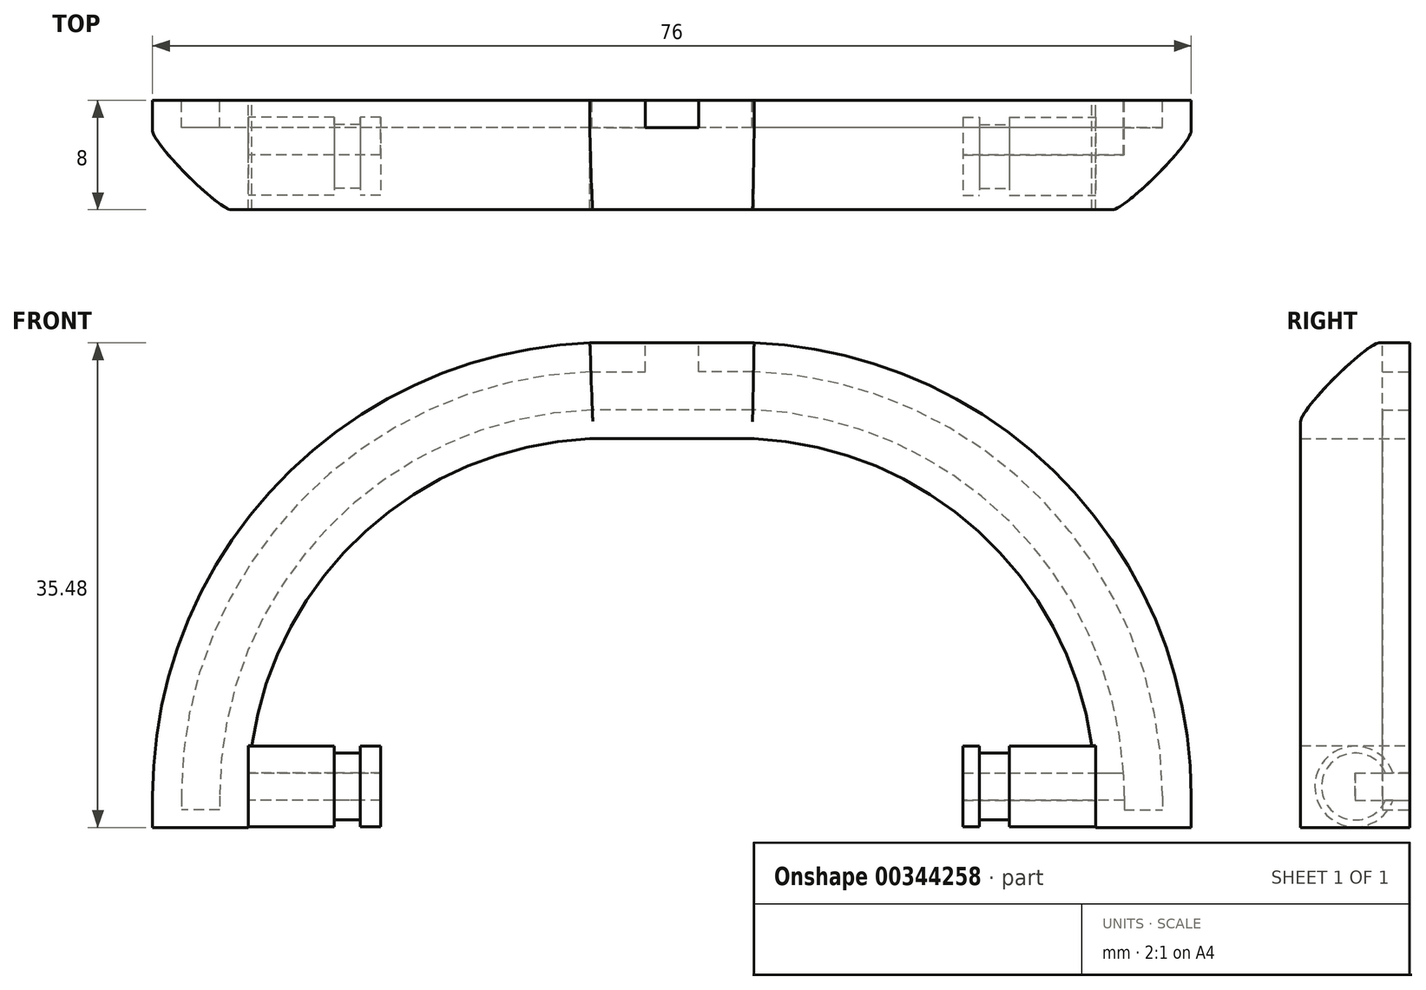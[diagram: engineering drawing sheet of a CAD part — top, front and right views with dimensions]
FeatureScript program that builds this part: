
annotation { "Feature Type Name" : "Feature", "Feature Type Description" : "" }
export const myFeature = defineFeature(function(context is Context, id is Id, definition is map)
    precondition{}
    {
        {
            var Q0;
            Q0=qCreatedBy(makeId("Front.planeOp"),FACE);
            var sketch = newSketch(context, id + "F0", { "sketchPlane" : qUnion([Q0])});
            skLineSegment(sketch, "E0.top", {"start": v(-4.75, 30.97) * mm, "end": v(4.75, 30.97) * mm});
            skPoint(sketch, "E0.middle", {"position": v(0, 0) * mm});
            skPoint(sketch, "E1", {"position": v(0, -2.5) * mm});
            skLineSegment(sketch, "E2", {"start": v(-38, -35.7) * mm, "end": v(-38, -38) * mm});
            skLineSegment(sketch, "E3", {"start": v(38, -35.7) * mm, "end": v(38, -38) * mm});
            skPoint(sketch, "E4.visualSharp", {"position": v(-38, -2.5) * mm});
            skArc(sketch, "E4.filletArc", {"start": v(-6, -2.52) * mm, "mid": v(-28.7, -12.65) * mm, "end": v(-38, -35.7) * mm});
            skPoint(sketch, "E5.visualSharp", {"position": v(38, -2.5) * mm});
            skArc(sketch, "E5.filletArc", {"start": v(38, -35.7) * mm, "mid": v(28.7, -12.66) * mm, "end": v(6.03, -2.52) * mm});
            skLineSegment(sketch, "E6", {"start": v(-31, -32) * mm, "end": v(-31, -38) * mm});
            skLineSegment(sketch, "E7", {"start": v(-38, -38) * mm, "end": v(-31, -38) * mm});
            skLineSegment(sketch, "E8", {"start": v(-4.75, 30.97) * mm, "end": v(-4.75, 9.5) * mm});
            skLineSegment(sketch, "E9", {"start": v(4.75, 9.47) * mm, "end": v(4.75, 30.97) * mm});
            skLineSegment(sketch, "E10.0", {"start": v(6.03, -2.52) * mm, "end": v(6, 9.48) * mm});
            skLineSegment(sketch, "E11.0", {"start": v(-6, 9.5) * mm, "end": v(-6, -2.52) * mm});
            skLineSegment(sketch, "E12", {"start": v(-6, 9.5) * mm, "end": v(-4.75, 9.5) * mm});
            skLineSegment(sketch, "E13", {"start": v(4.75, 9.47) * mm, "end": v(6, 9.48) * mm});
            skLineSegment(sketch, "E14", {"start": v(-6.02, -9.53) * mm, "end": v(6.02, -9.53) * mm});
            skLineSegment(sketch, "E15", {"start": v(-6, -2.52) * mm, "end": v(6.03, -2.52) * mm});
            skArc(sketch, "E16.0", {"start": v(-6.02, -9.53) * mm, "mid": v(-22.42, -16.31) * mm, "end": v(-30.74, -32) * mm});
            skLineSegment(sketch, "E17", {"start": v(-31, -32) * mm, "end": v(-30.74, -32) * mm});
            skLineSegment(sketch, "E18.MirrorCS", {"start": v(31, -32) * mm, "end": v(30.74, -32) * mm});
            skLineSegment(sketch, "E19.MirrorCS", {"start": v(38, -38) * mm, "end": v(31, -38) * mm});
            skLineSegment(sketch, "E20.MirrorCS", {"start": v(31, -32) * mm, "end": v(31, -38) * mm});
            skArc(sketch, "E21.MirrorCS", {"start": v(6.02, -9.53) * mm, "mid": v(22.42, -16.31) * mm, "end": v(30.74, -32) * mm});
            skSolve(sketch);
        }
        {
            var Q0;
            Q0=makeQuery(id+"F0.imprint","IMPRINT",FACE,{"disambiguationData":[TD([[makeQuery(id+"F0.imprint","IMPRINT",EDGE,{"derivedFrom":sQuery(id+"F0.wireOp",EDGE,"E2")}),1.0]])]});
            extrude(context, id + "F1", {"entities" : qUnion([Q0]), "depth" : 8 * mm});
        }
        {
            var Q0;
            Q0=makeQuery(id+"F1.opExtrude","CAP_EDGE",EDGE,{"disambiguationData":[OSD([sQuery(id+"F0.wireOp",EDGE,"E5.filletArc")])],"isStart":false});
            var Q1;
            Q1=makeQuery(id+"F1.opExtrude","CAP_EDGE",EDGE,{"disambiguationData":[OSD([sQuery(id+"F0.wireOp",EDGE,"E4.filletArc")])],"isStart":false});
            var Q2;
            Q2=makeQuery(id+"F1.opExtrude","CAP_EDGE",EDGE,{"disambiguationData":[OSD([sQuery(id+"F0.wireOp",EDGE,"E3")])],"isStart":false});
            var Q3;
            Q3=makeQuery(id+"F1.opExtrude","CAP_EDGE",EDGE,{"disambiguationData":[OSD([sQuery(id+"F0.wireOp",EDGE,"E2")])],"isStart":false});
            fillet(context, id + "F2", {"entities" : qUnion([Q0, Q1, Q2, Q3]), "radius" : 5.75 * mm, "tangentPropagation" : true, "rho" : 0.12, "crossSection" : FilletCrossSection.CONIC, "allowEdgeOverflow" : false});
        }
        {
            var Q0;
            Q0=makeQuery(id+"F1.opExtrude","SWEPT_FACE",FACE,{"disambiguationData":[OSD([sQuery(id+"F0.wireOp",EDGE,"E20.MirrorCS")])]});
            var sketch = newSketch(context, id + "F3", { "sketchPlane" : qUnion([Q0])});
            skLineSegment(sketch, "E22", {"start": v(0, -32) * mm, "end": v(8, -38) * mm, "construction": true});
            skCircle(sketch, "E23", {"center": v(4, -35) * mm, "radius": 2.95 * mm});
            skCircle(sketch, "E24", {"center": v(4, -35) * mm, "radius": 2.45 * mm});
            skSolve(sketch);
        }
        {
            var Q0;
            Q0=makeQuery(id+"F3.imprint","IMPRINT",FACE,{"disambiguationData":[TD([[makeQuery(id+"F3.imprint","IMPRINT",EDGE,{"derivedFrom":sQuery(id+"F3.wireOp",EDGE,"E23")}),1.0]])]});
            extrude(context, id + "F4", {"entities" : qUnion([Q0]), "operationType" : NewBodyOperationType.ADD, "depth" : 6.3 * mm});
        }
        {
            var Q0;
            Q0=makeQuery(id+"F3.imprint","IMPRINT",FACE,{"disambiguationData":[TD([[makeQuery(id+"F3.imprint","IMPRINT",EDGE,{"derivedFrom":sQuery(id+"F3.wireOp",EDGE,"E24")}),1.0]])]});
            extrude(context, id + "F5", {"entities" : qUnion([Q0]), "operationType" : NewBodyOperationType.ADD, "depth" : 9.7 * mm});
        }
        {
            var Q0;
            Q0=makeQuery(id+"F3.imprint","IMPRINT",FACE,{"disambiguationData":[TD([[makeQuery(id+"F3.imprint","IMPRINT",EDGE,{"derivedFrom":sQuery(id+"F3.wireOp",EDGE,"E23")}),1.0]])]});
            extrude(context, id + "F6", {"entities" : qUnion([Q0]), "operationType" : NewBodyOperationType.ADD, "depth" : 9.7 * mm, "hasSecondDirection" : true, "secondDirectionOppositeDirection" : false, "secondDirectionDepth" : 8.5 * mm});
        }
        {
            var Q0;
            Q0=makeQuery(id+"F1.opExtrude","SWEPT_FACE",FACE,{"disambiguationData":[OSD([sQuery(id+"F0.wireOp",EDGE,"E6")])]});
            var sketch = newSketch(context, id + "F7", { "sketchPlane" : qUnion([Q0])});
            skLineSegment(sketch, "E25", {"start": v(-8, -32) * mm, "end": v(0, -38) * mm, "construction": true});
            skCircle(sketch, "E26", {"center": v(-4, -35) * mm, "radius": 2.95 * mm});
            skCircle(sketch, "E27", {"center": v(-4, -35) * mm, "radius": 2.45 * mm});
            skSolve(sketch);
        }
        {
            var Q0;
            Q0=makeQuery(id+"F7.imprint","IMPRINT",FACE,{"disambiguationData":[TD([[makeQuery(id+"F7.imprint","IMPRINT",EDGE,{"derivedFrom":sQuery(id+"F7.wireOp",EDGE,"E26")}),1.0]])]});
            extrude(context, id + "F8", {"entities" : qUnion([Q0]), "operationType" : NewBodyOperationType.ADD, "depth" : 9.7 * mm, "hasSecondDirection" : true, "secondDirectionOppositeDirection" : false, "secondDirectionDepth" : 8.2 * mm});
        }
        {
            var Q0;
            Q0=makeQuery(id+"F7.imprint","IMPRINT",FACE,{"disambiguationData":[TD([[makeQuery(id+"F7.imprint","IMPRINT",EDGE,{"derivedFrom":sQuery(id+"F7.wireOp",EDGE,"E27")}),1.0]])]});
            extrude(context, id + "F9", {"entities" : qUnion([Q0]), "operationType" : NewBodyOperationType.ADD, "depth" : 9.7 * mm});
        }
        {
            var Q0;
            Q0=makeQuery(id+"F7.imprint","IMPRINT",FACE,{"disambiguationData":[TD([[makeQuery(id+"F7.imprint","IMPRINT",EDGE,{"derivedFrom":sQuery(id+"F7.wireOp",EDGE,"E26")}),1.0]])]});
            extrude(context, id + "F10", {"entities" : qUnion([Q0]), "operationType" : NewBodyOperationType.ADD, "depth" : 6.3 * mm});
        }
        {
            var Q0;
            Q0=makeQuery(id+"F0.imprint","IMPRINT",FACE,{"disambiguationData":[TD([[makeQuery(id+"F0.imprint","IMPRINT",EDGE,{"derivedFrom":sQuery(id+"F0.wireOp",EDGE,"E2")}),1.0]])]});
            var sketch = newSketch(context, id + "F11", { "sketchPlane" : qUnion([Q0])});
            skArc(sketch, "E28.0", {"start": v(35.9, -35.7) * mm, "mid": v(27.2, -14.12) * mm, "end": v(5.95, -4.62) * mm});
            skArc(sketch, "E29.0", {"start": v(33.1, -35.7) * mm, "mid": v(25.18, -16.06) * mm, "end": v(5.85, -7.42) * mm});
            skLineSegment(sketch, "E30", {"start": v(35.9, -35.7) * mm, "end": v(35.9, -36.7) * mm});
            skLineSegment(sketch, "E31", {"start": v(33.1, -35.7) * mm, "end": v(33.1, -36.7) * mm});
            skLineSegment(sketch, "E32", {"start": v(33.1, -36.7) * mm, "end": v(35.9, -36.7) * mm});
            skLineSegment(sketch, "E33.0", {"start": v(27, -32) * mm, "end": v(27, -38) * mm, "construction": true});
            skLineSegment(sketch, "E34.0", {"start": v(27, -36) * mm, "end": v(33.1, -36) * mm});
            skLineSegment(sketch, "E35", {"start": v(27, -36) * mm, "end": v(20.59, -36) * mm});
            skLineSegment(sketch, "E36", {"start": v(20.59, -36) * mm, "end": v(20.59, -34) * mm});
            skLineSegment(sketch, "E37", {"start": v(0, 0) * mm, "end": v(0, -4.62) * mm, "construction": true});
            skArc(sketch, "E38.MirrorCS", {"start": v(-33.1, -35.7) * mm, "mid": v(-25.18, -16.06) * mm, "end": v(-5.85, -7.42) * mm});
            skArc(sketch, "E39.MirrorCS", {"start": v(-35.9, -35.7) * mm, "mid": v(-27.2, -14.12) * mm, "end": v(-5.95, -4.62) * mm});
            skLineSegment(sketch, "E40.MirrorCS", {"start": v(-35.9, -35.7) * mm, "end": v(-35.9, -36.7) * mm});
            skLineSegment(sketch, "E41.MirrorCS", {"start": v(-33.1, -36.7) * mm, "end": v(-35.9, -36.7) * mm});
            skLineSegment(sketch, "E42.MirrorCS", {"start": v(-33.1, -35.7) * mm, "end": v(-33.1, -36.7) * mm});
            skLineSegment(sketch, "E43.MirrorCS", {"start": v(-27, -36) * mm, "end": v(-33.1, -36) * mm});
            skLineSegment(sketch, "E44.MirrorCS", {"start": v(-27, -34) * mm, "end": v(-33.05, -34) * mm});
            skLineSegment(sketch, "E45.MirrorCS", {"start": v(-27, -34) * mm, "end": v(-20.59, -34) * mm});
            skLineSegment(sketch, "E46.MirrorCS", {"start": v(-27, -36) * mm, "end": v(-20.59, -36) * mm});
            skLineSegment(sketch, "E47.MirrorCS", {"start": v(-20.59, -36) * mm, "end": v(-20.59, -34) * mm});
            skLineSegment(sketch, "E48", {"start": v(5.85, -7.42) * mm, "end": v(-5.85, -7.42) * mm});
            skLineSegment(sketch, "E49", {"start": v(5.95, -4.62) * mm, "end": v(1.95, -4.62) * mm});
            skLineSegment(sketch, "E50", {"start": v(1.95, -4.62) * mm, "end": v(1.95, 0) * mm});
            skLineSegment(sketch, "E51", {"start": v(-5.95, -4.62) * mm, "end": v(-1.95, -4.62) * mm});
            skLineSegment(sketch, "E52", {"start": v(-1.95, -4.62) * mm, "end": v(-1.95, 0) * mm});
            skLineSegment(sketch, "E53", {"start": v(-1.95, 0) * mm, "end": v(1.95, 0) * mm});
            skLineSegment(sketch, "E54", {"start": v(20.59, -34) * mm, "end": v(33.05, -34) * mm});
            skSolve(sketch);
        }
        {
            var Q0;
            Q0=makeQuery(id+"F11.imprint","IMPRINT",FACE,{"disambiguationData":[TD([[makeQuery(id+"F11.imprint","IMPRINT",EDGE,{"derivedFrom":sQuery(id+"F11.wireOp",EDGE,"E28.0")}),1.0]])]});
            var Q1;
            {var subQ0=sQuery(id+"F11.wireOp",EDGE,"E53");Q1=makeQuery(id+"F11.imprint","IMPRINT",FACE,{"disambiguationData":[TD([[makeQuery(id+"F11.imprint","IMPRINT",EDGE,{"derivedFrom":subQ0}),-1.0]])]});}
            extrude(context, id + "F12", {"entities" : qUnion([Q0, Q1]), "operationType" : NewBodyOperationType.REMOVE, "depth" : 2 * mm});
        }
        {
            var Q0;
            {var subQ1=sQuery(id+"F11.wireOp",EDGE,"E42.MirrorCS");var subQ6=sQuery(id+"F11.wireOp",EDGE,"E38.MirrorCS");var subQ9=makeQuery(id+"F11.imprint","INTERSECT",VERTEX,{"derivedFrom":[subQ6,subQ1]});Q0=makeQuery(id+"F11.imprint","IMPRINT",FACE,{"disambiguationData":[TD([[makeQuery(id+"F11.imprint","IMPRINT",EDGE,{"disambiguationData":[TD([[subQ9,-1.0]])],"derivedFrom":subQ6}),-1.0]])]});}
            var Q1;
            {var subQ0=sQuery(id+"F11.wireOp",EDGE,"E45.MirrorCS");Q1=makeQuery(id+"F11.imprint","IMPRINT",FACE,{"disambiguationData":[TD([[makeQuery(id+"F11.imprint","IMPRINT",EDGE,{"derivedFrom":subQ0}),-1.0]])]});}
            var Q2;
            {var subQ6=sQuery(id+"F11.wireOp",EDGE,"E35");Q2=makeQuery(id+"F11.imprint","IMPRINT",FACE,{"disambiguationData":[TD([[makeQuery(id+"F11.imprint","IMPRINT",EDGE,{"derivedFrom":subQ6}),-1.0]])]});}
            var Q3;
            {var subQ1=sQuery(id+"F11.wireOp",EDGE,"E31");var subQ6=sQuery(id+"F11.wireOp",EDGE,"E29.0");var subQ9=makeQuery(id+"F11.imprint","INTERSECT",VERTEX,{"derivedFrom":[subQ6,subQ1]});Q3=makeQuery(id+"F11.imprint","IMPRINT",FACE,{"disambiguationData":[TD([[makeQuery(id+"F11.imprint","IMPRINT",EDGE,{"disambiguationData":[TD([[subQ9,-1.0]])],"derivedFrom":subQ6}),1.0]])]});}
            extrude(context, id + "F13", {"entities" : qUnion([Q0, Q1, Q2, Q3]), "operationType" : NewBodyOperationType.REMOVE, "depth" : 4 * mm});
        }
    });
